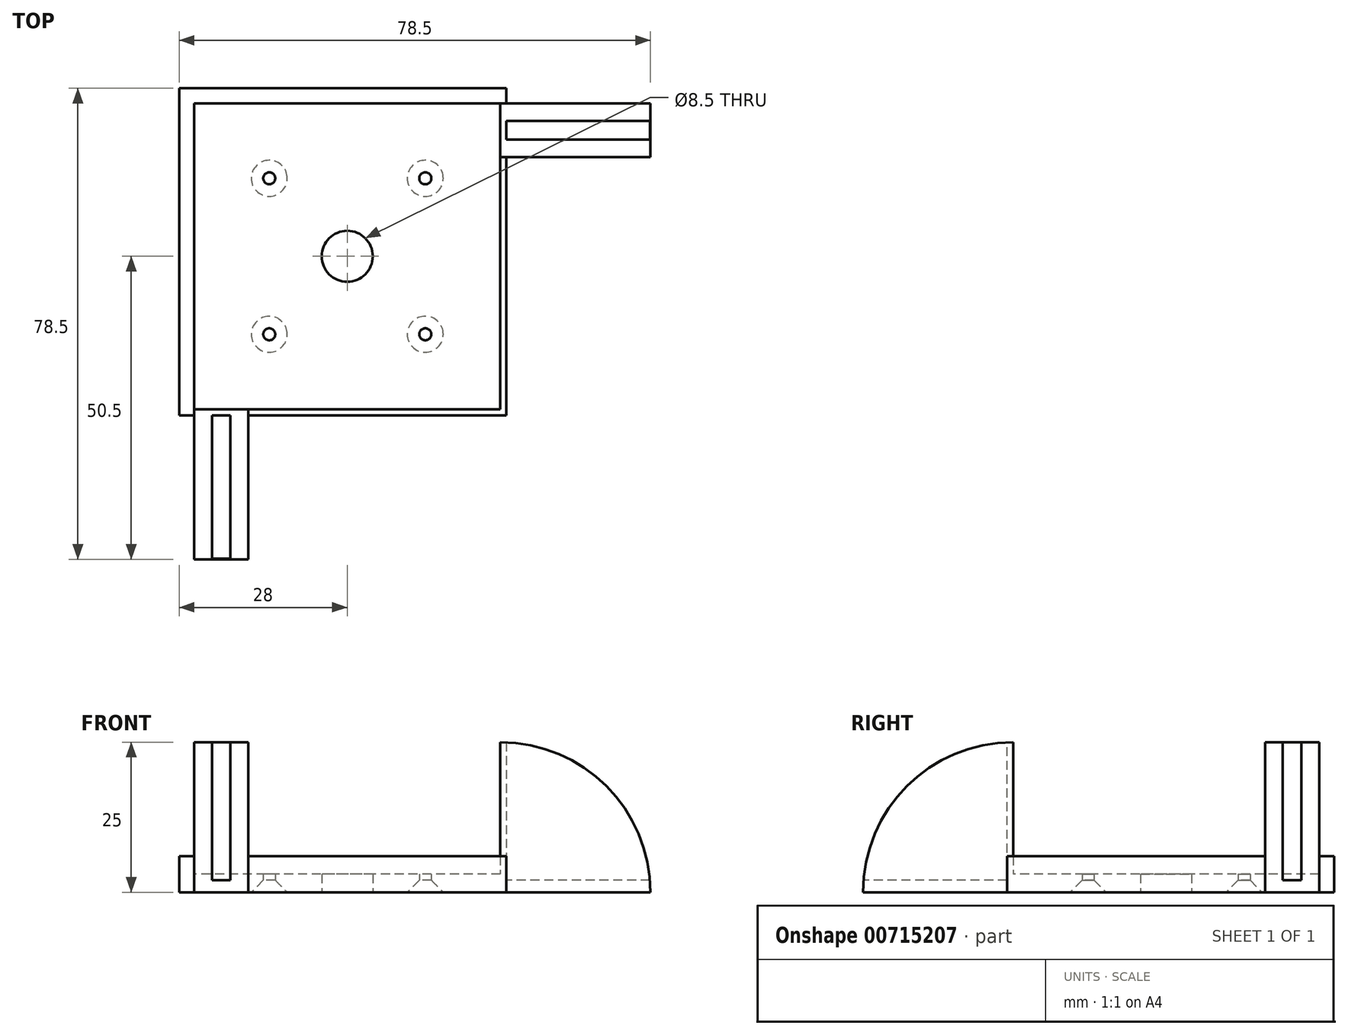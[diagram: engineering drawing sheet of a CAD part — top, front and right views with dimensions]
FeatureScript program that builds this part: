
annotation { "Feature Type Name" : "Feature", "Feature Type Description" : "" }
export const myFeature = defineFeature(function(context is Context, id is Id, definition is map)
    precondition{}
    {
        {
            var Q0;
            Q0=qCreatedBy(makeId("Top.planeOp"),FACE);
            var sketch = newSketch(context, id + "F0", { "sketchPlane" : qUnion([Q0])});
            skLineSegment(sketch, "E0.bottom", {"start": v(25.5, 25.5) * mm, "end": v(-25.5, 25.5) * mm});
            skLineSegment(sketch, "E0.top", {"start": v(25.5, -25.5) * mm, "end": v(-22.25, -25.5) * mm});
            skLineSegment(sketch, "E0.left", {"start": v(25.5, 25.5) * mm, "end": v(25.5, -25.5) * mm});
            skLineSegment(sketch, "E0.right", {"start": v(-25.5, 25.5) * mm, "end": v(-25.5, -25.5) * mm});
            skPoint(sketch, "E0.middle", {"position": v(0, 0) * mm});
            skLineSegment(sketch, "E1.0", {"start": v(28, 28) * mm, "end": v(-28, 28) * mm});
            skLineSegment(sketch, "E1.1", {"start": v(28, 28) * mm, "end": v(28, -28) * mm});
            skLineSegment(sketch, "E1.2", {"start": v(28, -28) * mm, "end": v(-22.25, -28) * mm});
            skLineSegment(sketch, "E1.3", {"start": v(-28, 28) * mm, "end": v(-28, -28) * mm});
            skCircle(sketch, "E2", {"center": v(-13, 13) * mm, "radius": 1 * mm});
            skLineSegment(sketch, "E3", {"start": v(0, 28) * mm, "end": v(0, -28) * mm, "construction": true});
            skLineSegment(sketch, "E4", {"start": v(-28, 0) * mm, "end": v(28, 0) * mm, "construction": true});
            skCircle(sketch, "E5.MirrorC", {"center": v(13, 13) * mm, "radius": 1 * mm});
            skCircle(sketch, "E6.MirrorC", {"center": v(13, -13) * mm, "radius": 1 * mm});
            skCircle(sketch, "E7.MirrorC", {"center": v(-13, -13) * mm, "radius": 1 * mm});
            skLineSegment(sketch, "E8.1", {"start": v(28, 30) * mm, "end": v(-30, 30) * mm});
            skLineSegment(sketch, "E9", {"start": v(28, 30) * mm, "end": v(28, 28) * mm});
            skLineSegment(sketch, "E10", {"start": v(-28, -28) * mm, "end": v(-30, -28) * mm});
            skLineSegment(sketch, "E11", {"start": v(28, 23.2) * mm, "end": v(28, 12.96) * mm});
            skLineSegment(sketch, "E12", {"start": v(28, 23.2) * mm, "end": v(28, 20) * mm});
            skLineSegment(sketch, "E13.trimOffspring", {"start": v(-25.25, -28) * mm, "end": v(-28, -28) * mm});
            skLineSegment(sketch, "E14", {"start": v(-25.5, -25.5) * mm, "end": v(-22.25, -25.5) * mm});
            skLineSegment(sketch, "E15", {"start": v(-25.25, -28) * mm, "end": v(-22.25, -28) * mm});
            skCircle(sketch, "E16", {"center": v(0, 0) * mm, "radius": 4.25 * mm});
            skLineSegment(sketch, "E17", {"start": v(-30, 30) * mm, "end": v(-30, -28) * mm});
            skSolve(sketch);
        }
        {
            var Q0;
            Q0=qCreatedBy(makeId("Top.planeOp"),FACE);
            var sketch = newSketch(context, id + "F1", { "sketchPlane" : qUnion([Q0])});
            skPoint(sketch, "E18.0", {"position": v(-25.5, -25.5) * mm});
            skLineSegment(sketch, "E19.bottom", {"start": v(-25.5, -25.5) * mm, "end": v(-16.5, -25.5) * mm});
            skLineSegment(sketch, "E19.top", {"start": v(-25.5, -50.5) * mm, "end": v(-16.5, -50.5) * mm});
            skLineSegment(sketch, "E19.left", {"start": v(-25.5, -25.5) * mm, "end": v(-25.5, -50.5) * mm});
            skLineSegment(sketch, "E19.right", {"start": v(-16.5, -25.5) * mm, "end": v(-16.5, -50.5) * mm});
            skLineSegment(sketch, "E20", {"start": v(-21, -50.5) * mm, "end": v(-21, -25.5) * mm, "construction": true});
            skLineSegment(sketch, "E21", {"start": v(-19.45, -25.5) * mm, "end": v(-19.45, -50.5) * mm});
            skLineSegment(sketch, "E22.MirrorCS", {"start": v(-22.55, -25.5) * mm, "end": v(-22.55, -50.5) * mm});
            skPoint(sketch, "E23.0", {"position": v(25.5, 25.5) * mm});
            skLineSegment(sketch, "E24.bottom", {"start": v(25.5, 25.5) * mm, "end": v(50.5, 25.5) * mm});
            skLineSegment(sketch, "E24.top", {"start": v(25.5, 16.5) * mm, "end": v(50.5, 16.5) * mm});
            skLineSegment(sketch, "E24.left", {"start": v(25.5, 25.5) * mm, "end": v(25.5, 16.5) * mm});
            skLineSegment(sketch, "E24.right", {"start": v(50.5, 25.5) * mm, "end": v(50.5, 16.5) * mm});
            skLineSegment(sketch, "E25", {"start": v(25.5, 21) * mm, "end": v(50.5, 21) * mm, "construction": true});
            skLineSegment(sketch, "E26", {"start": v(50.5, 22.55) * mm, "end": v(25.5, 22.55) * mm});
            skLineSegment(sketch, "E27.MirrorCS", {"start": v(50.5, 19.45) * mm, "end": v(25.5, 19.45) * mm});
            skSolve(sketch);
        }
        {
            var Q0;
            Q0=makeQuery(id+"F0.imprint","IMPRINT",FACE,{"disambiguationData":[TD([[makeQuery(id+"F0.imprint","IMPRINT",EDGE,{"derivedFrom":sQuery(id+"F0.wireOp",EDGE,"E0.bottom")}),1.0]])]});
            extrude(context, id + "F2", {"entities" : qUnion([Q0]), "depth" : 3 * mm, "offsetDistance" : 25 * mm});
        }
        {
            var Q0;
            Q0=makeQuery(id+"F0.imprint","IMPRINT",FACE,{"disambiguationData":[TD([[makeQuery(id+"F0.imprint","IMPRINT",EDGE,{"derivedFrom":sQuery(id+"F0.wireOp",EDGE,"E0.bottom")}),-1.0]])]});
            var Q1;
            {var subQ5=sQuery(id+"F0.wireOp",EDGE,"TI18WCdd-EPFC-hNpH-Rctt-afuqL8Zf6Xfq");Q1=makeQuery(id+"F0.imprint","IMPRINT",FACE,{"disambiguationData":[TD([[makeQuery(id+"F0.imprint","IMPRINT",EDGE,{"derivedFrom":subQ5}),-1.0]])]});}
            extrude(context, id + "F3", {"entities" : qUnion([Q0, Q1]), "operationType" : NewBodyOperationType.ADD, "depth" : 6 * mm, "offsetDistance" : 25 * mm});
        }
        {
            var Q0;
            Q0=makeQuery(id+"F2.opExtrude","CAP_EDGE",EDGE,{"disambiguationData":[OSD([sQuery(id+"F0.wireOp",EDGE,"E7.MirrorC")])],"isStart":true});
            var Q1;
            Q1=makeQuery(id+"F2.opExtrude","CAP_EDGE",EDGE,{"disambiguationData":[OSD([sQuery(id+"F0.wireOp",EDGE,"E6.MirrorC")])],"isStart":true});
            var Q2;
            Q2=makeQuery(id+"F2.opExtrude","CAP_EDGE",EDGE,{"disambiguationData":[OSD([sQuery(id+"F0.wireOp",EDGE,"E5.MirrorC")])],"isStart":true});
            var Q3;
            Q3=makeQuery(id+"F2.opExtrude","CAP_EDGE",EDGE,{"disambiguationData":[OSD([sQuery(id+"F0.wireOp",EDGE,"E2")])],"isStart":true});
            chamfer(context, id + "F4", {"entities" : qUnion([Q0, Q1, Q2, Q3]), "width" : 2 * mm, "tangentPropagation" : true});
        }
        {
            var Q0;
            Q0=makeQuery(id+"FIbiUBh41szAzK7_1.boolean.opBoolean","MERGE",FACE,{"derivedFrom":[makeQuery(id+"F3.opExtrude","SWEPT_FACE",FACE,{"disambiguationData":[OSD([sQuery(id+"F0.wireOp",EDGE,"E1.2"),sQuery(id+"F0.wireOp",EDGE,"E13.trimOffspring"),sQuery(id+"F0.wireOp",EDGE,"E15")])]}),makeQuery(id+"FIbiUBh41szAzK7_1.opExtrude","SWEPT_FACE",FACE,{"disambiguationData":[OSD([sQuery(id+"F0.wireOp",EDGE,"E10")])]})]});
            extrude(context, id + "F5", {"entities" : qUnion([Q0]), "operationType" : NewBodyOperationType.REMOVE, "oppositeDirection" : true, "depth" : 1.5 * mm, "offsetDistance" : 25 * mm});
        }
        {
            var Q0;
            Q0=makeQuery(id+"FIbiUBh41szAzK7_1.boolean.opBoolean","MERGE",FACE,{"derivedFrom":[makeQuery(id+"F3.opExtrude","SWEPT_FACE",FACE,{"disambiguationData":[OSD([sQuery(id+"F0.wireOp",EDGE,"E1.1"),sQuery(id+"F0.wireOp",EDGE,"E11"),sQuery(id+"F0.wireOp",EDGE,"E12")])]}),makeQuery(id+"FIbiUBh41szAzK7_1.opExtrude","SWEPT_FACE",FACE,{"disambiguationData":[OSD([sQuery(id+"F0.wireOp",EDGE,"E9")])]})]});
            extrude(context, id + "F6", {"entities" : qUnion([Q0]), "operationType" : NewBodyOperationType.REMOVE, "oppositeDirection" : true, "depth" : 1.5 * mm, "offsetDistance" : 25 * mm});
        }
        {
            var Q0;
            {var subQ0=sQuery(id+"F1.wireOp",EDGE,"E19.right");Q0=makeQuery(id+"F1.imprint","IMPRINT",FACE,{"disambiguationData":[TD([[makeQuery(id+"F1.imprint","IMPRINT",EDGE,{"derivedFrom":subQ0}),-1.0]])]});}
            var Q1;
            {var subQ0=sQuery(id+"F1.wireOp",EDGE,"E19.left");Q1=makeQuery(id+"F1.imprint","IMPRINT",FACE,{"disambiguationData":[TD([[makeQuery(id+"F1.imprint","IMPRINT",EDGE,{"derivedFrom":subQ0}),1.0]])]});}
            var Q2;
            {var subQ0=sQuery(id+"F1.wireOp",EDGE,"E24.top");Q2=makeQuery(id+"F1.imprint","IMPRINT",FACE,{"disambiguationData":[TD([[makeQuery(id+"F1.imprint","IMPRINT",EDGE,{"derivedFrom":subQ0}),1.0]])]});}
            var Q3;
            {var subQ0=sQuery(id+"F1.wireOp",EDGE,"E24.bottom");Q3=makeQuery(id+"F1.imprint","IMPRINT",FACE,{"disambiguationData":[TD([[makeQuery(id+"F1.imprint","IMPRINT",EDGE,{"derivedFrom":subQ0}),-1.0]])]});}
            extrude(context, id + "F7", {"entities" : qUnion([Q0, Q1, Q2, Q3]), "operationType" : NewBodyOperationType.ADD, "depth" : 25 * mm, "offsetDistance" : 25 * mm});
        }
        {
            var Q0;
            {var subQ0=sQuery(id+"F1.wireOp",EDGE,"E21");Q0=makeQuery(id+"F1.imprint","IMPRINT",FACE,{"disambiguationData":[TD([[makeQuery(id+"F1.imprint","IMPRINT",EDGE,{"derivedFrom":subQ0}),-1.0]])]});}
            var Q1;
            {var subQ0=sQuery(id+"F1.wireOp",EDGE,"E26");Q1=makeQuery(id+"F1.imprint","IMPRINT",FACE,{"disambiguationData":[TD([[makeQuery(id+"F1.imprint","IMPRINT",EDGE,{"derivedFrom":subQ0}),1.0]])]});}
            extrude(context, id + "F8", {"entities" : qUnion([Q0, Q1]), "operationType" : NewBodyOperationType.ADD, "depth" : 2 * mm, "offsetDistance" : 25 * mm});
        }
        {
            var Q0;
            {var subQ1=sQuery(id+"F1.wireOp",EDGE,"E21");var subQ3=sQuery(id+"F0.wireOp",EDGE,"E15");var subQ4=sQuery(id+"F0.wireOp",EDGE,"E13.trimOffspring");var subQ5=sQuery(id+"F0.wireOp",EDGE,"E1.2");var subQ6=sQuery(id+"F0.wireOp",EDGE,"E14");var subQ7=sQuery(id+"F0.wireOp",EDGE,"E0.top");Q0=makeQuery(id+"F7.boolean.opBoolean","SPLIT",FACE,{"disambiguationData":[TD([makeQuery(id+"F7.opExtrude","SWEPT_FACE",FACE,{"disambiguationData":[OSD([subQ1])]})])],"derivedFrom":makeQuery(id+"F3.opExtrude","CAP_FACE",FACE,{"disambiguationData":[OSD([sQuery(id+"F0.wireOp",EDGE,"E0.bottom"),subQ7,sQuery(id+"F0.wireOp",EDGE,"E0.left"),sQuery(id+"F0.wireOp",EDGE,"E0.right"),sQuery(id+"F0.wireOp",EDGE,"E1.0"),sQuery(id+"F0.wireOp",EDGE,"E1.1"),subQ5,sQuery(id+"F0.wireOp",EDGE,"E1.3"),sQuery(id+"F0.wireOp",EDGE,"E11"),sQuery(id+"F0.wireOp",EDGE,"E12"),subQ4,subQ6,subQ3])],"isStart":false})});}
            var Q1;
            {var subQ1=sQuery(id+"F1.wireOp",EDGE,"E26");var subQ2=sQuery(id+"F0.wireOp",EDGE,"E12");var subQ3=sQuery(id+"F0.wireOp",EDGE,"E11");var subQ4=sQuery(id+"F0.wireOp",EDGE,"E1.1");var subQ6=sQuery(id+"F0.wireOp",EDGE,"E0.left");Q1=makeQuery(id+"F7.boolean.opBoolean","SPLIT",FACE,{"disambiguationData":[TD([makeQuery(id+"F7.opExtrude","SWEPT_FACE",FACE,{"disambiguationData":[OSD([subQ1])]})])],"derivedFrom":makeQuery(id+"F3.opExtrude","CAP_FACE",FACE,{"disambiguationData":[OSD([sQuery(id+"F0.wireOp",EDGE,"E0.bottom"),sQuery(id+"F0.wireOp",EDGE,"E0.top"),subQ6,sQuery(id+"F0.wireOp",EDGE,"E0.right"),sQuery(id+"F0.wireOp",EDGE,"E1.0"),subQ4,sQuery(id+"F0.wireOp",EDGE,"E1.2"),sQuery(id+"F0.wireOp",EDGE,"E1.3"),subQ3,subQ2,sQuery(id+"F0.wireOp",EDGE,"E13.trimOffspring"),sQuery(id+"F0.wireOp",EDGE,"E14"),sQuery(id+"F0.wireOp",EDGE,"E15")])],"isStart":false})});}
            var Q2;
            Q2=makeQuery(id+"F7.opExtrude","CAP_FACE",FACE,{"disambiguationData":[OSD([sQuery(id+"F1.wireOp",EDGE,"E19.bottom"),sQuery(id+"F1.wireOp",EDGE,"E19.top"),sQuery(id+"F1.wireOp",EDGE,"E19.left"),sQuery(id+"F1.wireOp",EDGE,"E22.MirrorCS")])],"isStart":false});
            var Q3;
            Q3=makeQuery(id+"F2.opExtrude","SWEPT_BODY",BODY,{"disambiguationData":[OSD([sQuery(id+"F0.wireOp",EDGE,"E0.bottom"),sQuery(id+"F0.wireOp",EDGE,"E0.top"),sQuery(id+"F0.wireOp",EDGE,"E0.left"),sQuery(id+"F0.wireOp",EDGE,"E0.right"),sQuery(id+"F0.wireOp",EDGE,"E2"),sQuery(id+"F0.wireOp",EDGE,"E5.MirrorC"),sQuery(id+"F0.wireOp",EDGE,"E6.MirrorC"),sQuery(id+"F0.wireOp",EDGE,"E7.MirrorC"),sQuery(id+"F0.wireOp",EDGE,"E14"),sQuery(id+"F0.wireOp",EDGE,"E16")])]});
            extrude(context, id + "F9", {"entities" : qUnion([Q0, Q1]), "operationType" : NewBodyOperationType.ADD, "endBound" : BoundingType.UP_TO_SURFACE, "depth" : 25 * mm, "endBoundEntityFace" : qUnion([Q2]), "endBoundEntityBody" : qUnion([Q3]), "offsetDistance" : 25 * mm});
        }
        {
            var Q0;
            {var subQ0=sQuery(id+"F1.wireOp",EDGE,"E19.top");Q0=makeQuery(id+"F7.opExtrude","CAP_EDGE",EDGE,{"disambiguationData":[OSD([subQ0]),TDD([makeQuery(id+"F1.imprint","IMPRINT",EDGE,{"disambiguationData":[TD([[makeQuery(id+"F1.imprint","INTERSECT",VERTEX,{"derivedFrom":[subQ0,sQuery(id+"F1.wireOp",EDGE,"E19.left")]}),-1.0]])],"derivedFrom":subQ0})])],"isStart":false});}
            var Q1;
            {var subQ0=sQuery(id+"F1.wireOp",EDGE,"E19.top");Q1=makeQuery(id+"F7.opExtrude","CAP_EDGE",EDGE,{"disambiguationData":[OSD([subQ0]),TDD([makeQuery(id+"F1.imprint","IMPRINT",EDGE,{"disambiguationData":[TD([[makeQuery(id+"F1.imprint","INTERSECT",VERTEX,{"derivedFrom":[subQ0,sQuery(id+"F1.wireOp",EDGE,"E19.right")]}),1.0]])],"derivedFrom":subQ0})])],"isStart":false});}
            var Q2;
            {var subQ0=sQuery(id+"F1.wireOp",EDGE,"E24.right");Q2=makeQuery(id+"F7.opExtrude","CAP_EDGE",EDGE,{"disambiguationData":[OSD([subQ0]),TDD([makeQuery(id+"F1.imprint","IMPRINT",EDGE,{"disambiguationData":[TD([[makeQuery(id+"F1.imprint","INTERSECT",VERTEX,{"derivedFrom":[sQuery(id+"F1.wireOp",EDGE,"E24.bottom"),subQ0]}),-1.0]])],"derivedFrom":subQ0})])],"isStart":false});}
            fillet(context, id + "F10", {"entities" : qUnion([Q0, Q1, Q2]), "radius" : 25 * mm, "tangentPropagation" : true, "allowEdgeOverflow" : false});
        }
    });
